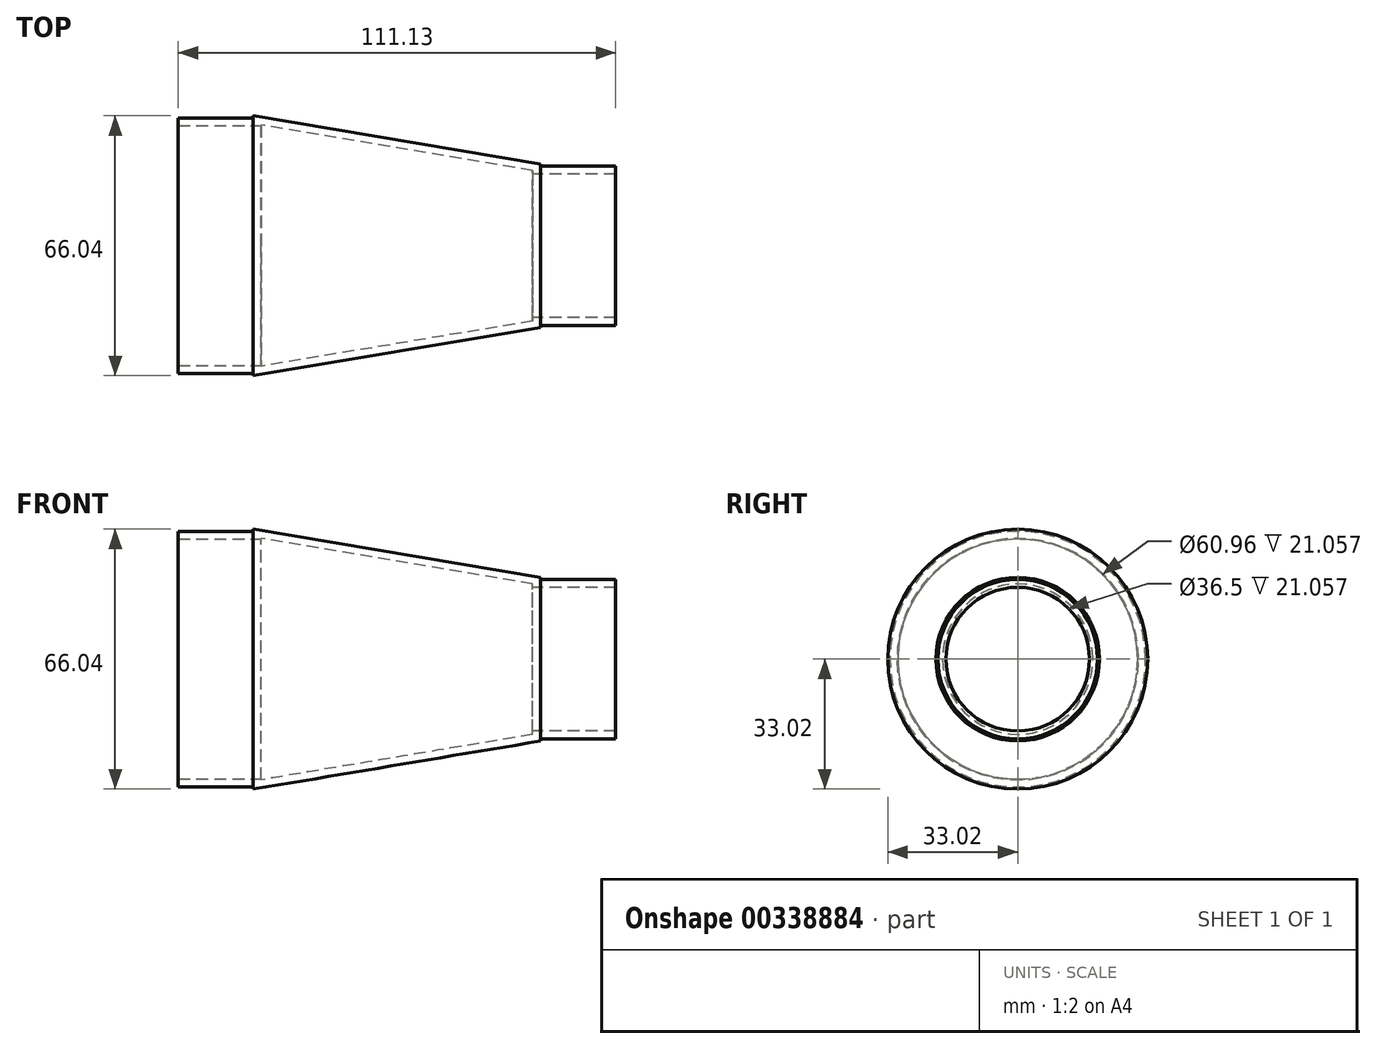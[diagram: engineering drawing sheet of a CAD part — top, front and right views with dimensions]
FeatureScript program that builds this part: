
annotation { "Feature Type Name" : "Feature", "Feature Type Description" : "" }
export const myFeature = defineFeature(function(context is Context, id is Id, definition is map)
    precondition{}
    {
        {
            var Q0;
            Q0=qCreatedBy(makeId("Right.planeOp"),FACE);
            var sketch = newSketch(context, id + "F0", { "sketchPlane" : qUnion([Q0])});
            skCircle(sketch, "E0", {"center": v(0, 0) * mm, "radius": 33.02 * mm});
            skSolve(sketch);
        }
        {
            var Q0;
            Q0=qCreatedBy(makeId("Right.planeOp"),FACE);
            cPlane(context, id + "F1", {"entities" : qUnion([Q0]), "cplaneType" : CPlaneType.OFFSET, "offset" : 73.02 * mm, "width" : 152.4 * mm, "height" : 152.4 * mm});
        }
        {
            var Q0;
            Q0=qCreatedBy(id+"F1.planeOp",FACE);
            var sketch = newSketch(context, id + "F2", { "sketchPlane" : qUnion([Q0])});
            skCircle(sketch, "E1", {"center": v(0, 0) * mm, "radius": 20.79 * mm});
            skSolve(sketch);
        }
        {
            var Q0;
            Q0=makeQuery(id+"F2.imprint","IMPRINT",FACE,{"disambiguationData":[TD([[makeQuery(id+"F2.imprint","IMPRINT",EDGE,{"derivedFrom":sQuery(id+"F2.wireOp",EDGE,"E1")}),1.0]])]});
            var Q1;
            Q1=makeQuery(id+"F0.imprint","IMPRINT",FACE,{"disambiguationData":[TD([[makeQuery(id+"F0.imprint","IMPRINT",EDGE,{"derivedFrom":sQuery(id+"F0.wireOp",EDGE,"E0")}),1.0]])]});
            loft(context, id + "F3", {"sheetProfilesArray" : [{ "sheetProfileEntities" : qUnion([Q0]) }, { "sheetProfileEntities" : qUnion([Q1]) }]});
        }
        {
            var Q0;
            Q0=makeQuery(id+"F3.opLoft","CAP_FACE",FACE,{"disambiguationData":[OSD([makeQuery(id+"F0.imprint","IMPRINT",FACE,{"disambiguationData":[TD([[makeQuery(id+"F0.imprint","IMPRINT",EDGE,{"derivedFrom":sQuery(id+"F0.wireOp",EDGE,"E0")}),1.0]])]})])],"isStart":true});
            var sketch = newSketch(context, id + "F4", { "sketchPlane" : qUnion([Q0])});
            skCircle(sketch, "E2", {"center": v(0, 0) * mm, "radius": 32.49 * mm});
            skSolve(sketch);
        }
        {
            var Q0;
            Q0=makeQuery(id+"F4.imprint","IMPRINT",FACE,{"disambiguationData":[TD([[makeQuery(id+"F4.imprint","IMPRINT",EDGE,{"derivedFrom":sQuery(id+"F4.wireOp",EDGE,"E2")}),1.0]])]});
            extrude(context, id + "F5", {"entities" : qUnion([Q0]), "operationType" : NewBodyOperationType.ADD, "depth" : 19.05 * mm});
        }
        {
            var Q0;
            Q0=makeQuery(id+"F3.opLoft","CAP_FACE",FACE,{"disambiguationData":[OSD([makeQuery(id+"F2.imprint","IMPRINT",FACE,{"disambiguationData":[TD([[makeQuery(id+"F2.imprint","IMPRINT",EDGE,{"derivedFrom":sQuery(id+"F2.wireOp",EDGE,"E1")}),1.0]])]})])],"isStart":true});
            var sketch = newSketch(context, id + "F6", { "sketchPlane" : qUnion([Q0])});
            skCircle(sketch, "E3", {"center": v(0, 0) * mm, "radius": 20.26 * mm});
            skSolve(sketch);
        }
        {
            var Q0;
            Q0=makeQuery(id+"F6.imprint","IMPRINT",FACE,{"disambiguationData":[TD([[makeQuery(id+"F6.imprint","IMPRINT",EDGE,{"derivedFrom":sQuery(id+"F6.wireOp",EDGE,"E3")}),1.0]])]});
            extrude(context, id + "F7", {"entities" : qUnion([Q0]), "operationType" : NewBodyOperationType.ADD, "depth" : 19.05 * mm});
        }
        {
            var Q0;
            Q0=makeQuery(id+"F7.opExtrude","CAP_FACE",FACE,{"disambiguationData":[OSD([sQuery(id+"F6.wireOp",EDGE,"E3")])],"isStart":false});
            var Q1;
            Q1=makeQuery(id+"F5.opExtrude","CAP_FACE",FACE,{"disambiguationData":[OSD([sQuery(id+"F4.wireOp",EDGE,"E2")])],"isStart":false});
            shell(context, id + "F8", {"entities" : qUnion([Q0, Q1]), "thickness" : 2 * mm});
        }
    });
